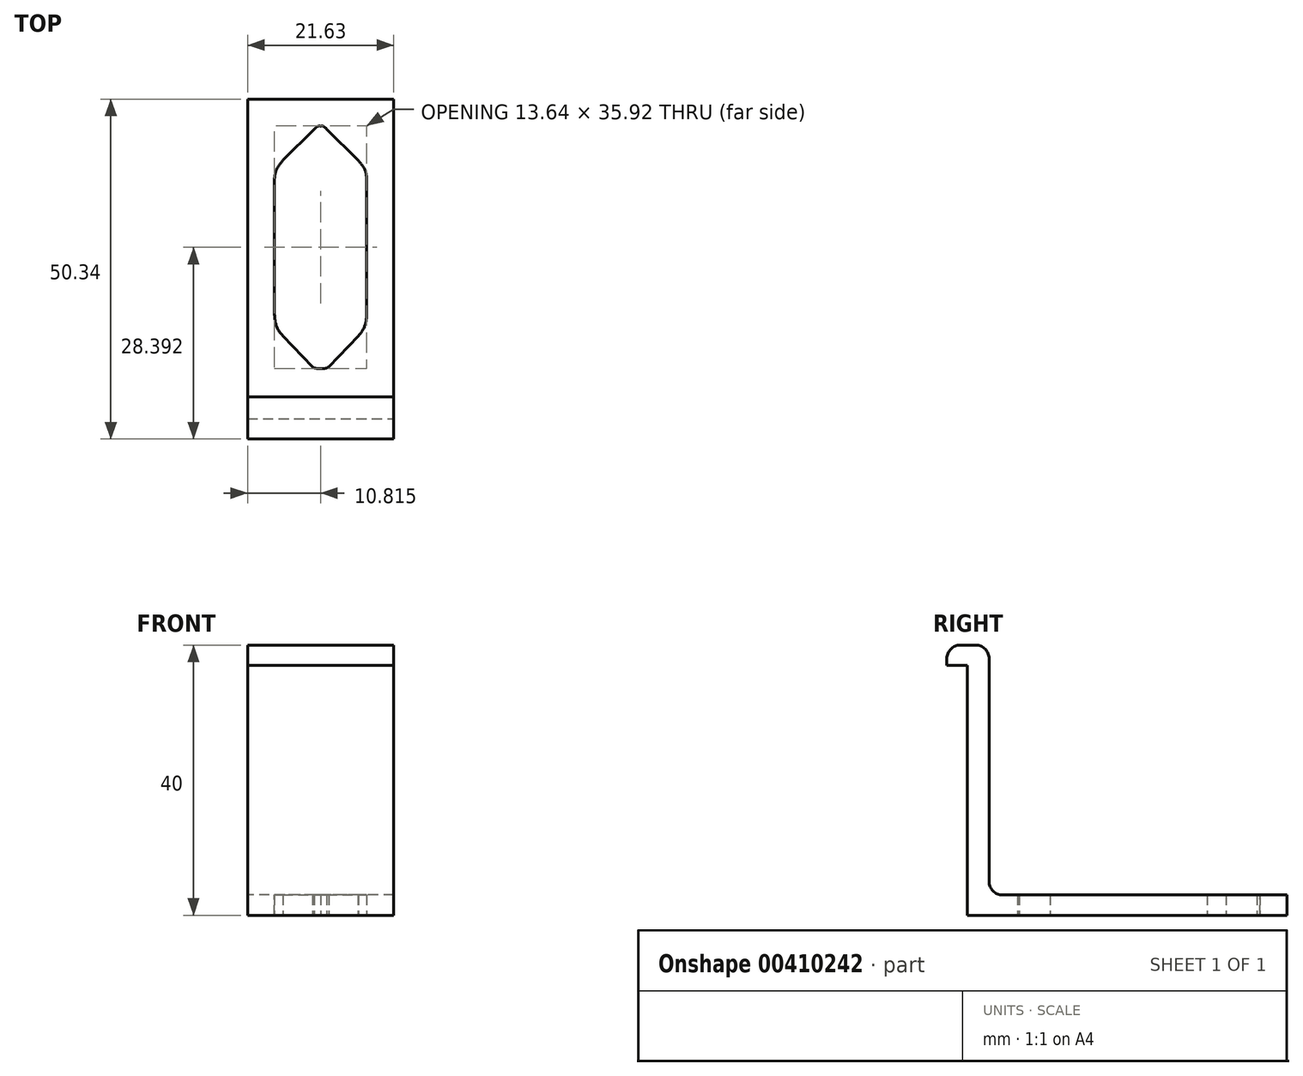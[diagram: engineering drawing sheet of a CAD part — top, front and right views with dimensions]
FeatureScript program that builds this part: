
annotation { "Feature Type Name" : "Feature", "Feature Type Description" : "" }
export const myFeature = defineFeature(function(context is Context, id is Id, definition is map)
    precondition{}
    {
        {
            var Q0;
            Q0=qCreatedBy(makeId("Top.planeOp"),FACE);
            var sketch = newSketch(context, id + "F0", { "sketchPlane" : qUnion([Q0])});
            skLineSegment(sketch, "E0", {"start": v(60.72, -23.6) * mm, "end": v(60.72, -19.6) * mm, "construction": true});
            skFitSpline(sketch, "E1", {"points": [v(60.72, 16.31) * mm, v(61.64, 15.85) * mm], "startDerivative": vector(1.57, 0.08) * mm, "endDerivative": vector(1.53, -1.37) * mm});
            skLineSegment(sketch, "E2", {"start": v(61.64, 15.85) * mm, "end": v(66.27, 11.3) * mm});
            skFitSpline(sketch, "E3", {"points": [v(66.27, 11.3) * mm, v(67.53, 8.52) * mm], "startDerivative": vector(2.41, -3.3) * mm, "endDerivative": vector(0.3, -4.44) * mm});
            skLineSegment(sketch, "E4", {"start": v(67.53, 8.52) * mm, "end": v(67.53, -11.27) * mm});
            skFitSpline(sketch, "E5", {"points": [v(67.53, -11.27) * mm, v(66.32, -14.75) * mm], "startDerivative": vector(0.03, -4.08) * mm, "endDerivative": vector(-3.06, -3.36) * mm});
            skLineSegment(sketch, "E6", {"start": v(66.32, -14.75) * mm, "end": v(61.93, -19.32) * mm});
            skFitSpline(sketch, "E7", {"points": [v(61.93, -19.32) * mm, v(60.72, -19.6) * mm], "startDerivative": vector(-1.02, -0.93) * mm, "endDerivative": vector(-1.06, -0.03) * mm});
            skLineSegment(sketch, "E8.MirrorCS", {"start": v(53.9, 8.52) * mm, "end": v(53.9, -11.27) * mm});
            skLineSegment(sketch, "E9.MirrorCS", {"start": v(59.79, 15.85) * mm, "end": v(55.16, 11.3) * mm});
            skFitSpline(sketch, "E10.MirrorCS", {"points": [v(60.72, 16.31) * mm, v(59.79, 15.85) * mm], "startDerivative": vector(-1.57, 0.08) * mm, "endDerivative": vector(-1.53, -1.37) * mm});
            skFitSpline(sketch, "E11.MirrorCS", {"points": [v(55.16, 11.3) * mm, v(53.9, 8.52) * mm], "startDerivative": vector(-2.41, -3.3) * mm, "endDerivative": vector(-0.3, -4.44) * mm});
            skFitSpline(sketch, "E12.MirrorCS", {"points": [v(53.9, -11.27) * mm, v(55.11, -14.75) * mm], "startDerivative": vector(-0.03, -4.08) * mm, "endDerivative": vector(3.06, -3.36) * mm});
            skLineSegment(sketch, "E13.MirrorCS", {"start": v(55.11, -14.75) * mm, "end": v(59.5, -19.32) * mm});
            skFitSpline(sketch, "E14.MirrorCS", {"points": [v(59.5, -19.32) * mm, v(60.72, -19.6) * mm], "startDerivative": vector(1.02, -0.93) * mm, "endDerivative": vector(1.06, -0.03) * mm});
            skLineSegment(sketch, "E15", {"start": v(67.53, -1.37) * mm, "end": v(71.53, -1.37) * mm, "construction": true});
            skLineSegment(sketch, "E16", {"start": v(71.53, -23.03) * mm, "end": v(71.53, 20.31) * mm});
            skLineSegment(sketch, "E17", {"start": v(71.53, 20.31) * mm, "end": v(60.72, 20.31) * mm});
            skLineSegment(sketch, "E18.MirrorCS", {"start": v(49.9, -23.03) * mm, "end": v(49.9, 20.31) * mm});
            skLineSegment(sketch, "E19.MirrorCS", {"start": v(49.9, 20.31) * mm, "end": v(60.72, 20.31) * mm});
            skLineSegment(sketch, "E20", {"start": v(60.72, 16.31) * mm, "end": v(60.72, 20.31) * mm, "construction": true});
            skLineSegment(sketch, "E21", {"start": v(60.72, -19.6) * mm, "end": v(60.72, 16.31) * mm, "construction": true});
            skLineSegment(sketch, "E22.top", {"start": v(49.9, -27.03) * mm, "end": v(71.53, -27.03) * mm});
            skLineSegment(sketch, "E22.left", {"start": v(49.9, -23.03) * mm, "end": v(49.9, -23.78) * mm});
            skLineSegment(sketch, "E22.right", {"start": v(71.53, -23.03) * mm, "end": v(71.53, -27.03) * mm});
            skLineSegment(sketch, "E23", {"start": v(49.9, -23.78) * mm, "end": v(71.53, -23.78) * mm});
            skLineSegment(sketch, "E24", {"start": v(49.9, -23.78) * mm, "end": v(49.9, -27.03) * mm});
            skSolve(sketch);
        }
        {
            var Q0;
            Q0=makeQuery(id+"F0.imprint","IMPRINT",FACE,{"disambiguationData":[TD([[makeQuery(id+"F0.imprint","IMPRINT",EDGE,{"derivedFrom":sQuery(id+"F0.wireOp",EDGE,"E1")}),1.0]])]});
            var Q1;
            {var subQ0=sQuery(id+"F0.wireOp",EDGE,"E22.top");Q1=makeQuery(id+"F0.imprint","IMPRINT",FACE,{"disambiguationData":[TD([[makeQuery(id+"F0.imprint","IMPRINT",EDGE,{"derivedFrom":subQ0}),1.0]])]});}
            extrude(context, id + "F1", {"entities" : qUnion([Q0, Q1]), "depth" : 3 * mm});
        }
        {
            var Q0;
            {var subQ0=sQuery(id+"F0.wireOp",EDGE,"E22.top");Q0=makeQuery(id+"F0.imprint","IMPRINT",FACE,{"disambiguationData":[TD([[makeQuery(id+"F0.imprint","IMPRINT",EDGE,{"derivedFrom":subQ0}),1.0]])]});}
            extrude(context, id + "F2", {"entities" : qUnion([Q0]), "operationType" : NewBodyOperationType.ADD, "depth" : 40 * mm});
        }
        {
            var Q0;
            {var subQ0=sQuery(id+"F0.wireOp",EDGE,"E22.top");Q0=makeQuery(id+"F2.boolean.opBoolean","MERGE",FACE,{"derivedFrom":[makeQuery(id+"F1.opExtrude","SWEPT_FACE",FACE,{"disambiguationData":[OSD([subQ0])]}),makeQuery(id+"F2.opExtrude","SWEPT_FACE",FACE,{"disambiguationData":[OSD([subQ0])]})]});}
            var sketch = newSketch(context, id + "F3", { "sketchPlane" : qUnion([Q0])});
            skLineSegment(sketch, "E25.bottom", {"start": v(49.9, 40) * mm, "end": v(71.53, 40) * mm});
            skLineSegment(sketch, "E25.top", {"start": v(49.9, 37) * mm, "end": v(71.53, 37) * mm});
            skLineSegment(sketch, "E25.left", {"start": v(49.9, 40) * mm, "end": v(49.9, 37) * mm});
            skLineSegment(sketch, "E25.right", {"start": v(71.53, 40) * mm, "end": v(71.53, 37) * mm});
            skSolve(sketch);
        }
        {
            var Q0;
            Q0 = qSketchRegion(id + "F3", true);
            extrude(context, id + "F4", {"entities" : qUnion([Q0]), "operationType" : NewBodyOperationType.ADD, "depth" : 3 * mm});
        }
        {
            var Q0;
            Q0=makeQuery(id+"F4.opExtrude","CAP_EDGE",EDGE,{"disambiguationData":[OSD([sQuery(id+"F3.wireOp",EDGE,"E25.bottom")])],"isStart":false});
            var Q1;
            Q1=makeQuery(id+"F2.opExtrude","CAP_EDGE",EDGE,{"disambiguationData":[OSD([sQuery(id+"F0.wireOp",EDGE,"E23")])],"isStart":false});
            var Q2;
            Q2=makeQuery(id+"F2.boolean.opBoolean","INTERSECT",EDGE,{"derivedFrom":[makeQuery(id+"F1.opExtrude","CAP_FACE",FACE,{"disambiguationData":[OSD([sQuery(id+"F0.wireOp",EDGE,"E1"),sQuery(id+"F0.wireOp",EDGE,"E2"),sQuery(id+"F0.wireOp",EDGE,"E3"),sQuery(id+"F0.wireOp",EDGE,"E4"),sQuery(id+"F0.wireOp",EDGE,"E5"),sQuery(id+"F0.wireOp",EDGE,"E6"),sQuery(id+"F0.wireOp",EDGE,"E7"),sQuery(id+"F0.wireOp",EDGE,"E8.MirrorCS"),sQuery(id+"F0.wireOp",EDGE,"E9.MirrorCS"),sQuery(id+"F0.wireOp",EDGE,"E10.MirrorCS"),sQuery(id+"F0.wireOp",EDGE,"E11.MirrorCS"),sQuery(id+"F0.wireOp",EDGE,"E12.MirrorCS"),sQuery(id+"F0.wireOp",EDGE,"E13.MirrorCS"),sQuery(id+"F0.wireOp",EDGE,"E14.MirrorCS"),sQuery(id+"F0.wireOp",EDGE,"E16"),sQuery(id+"F0.wireOp",EDGE,"E17"),sQuery(id+"F0.wireOp",EDGE,"E18.MirrorCS"),sQuery(id+"F0.wireOp",EDGE,"E19.MirrorCS"),sQuery(id+"F0.wireOp",EDGE,"E22.top"),sQuery(id+"F0.wireOp",EDGE,"E22.left"),sQuery(id+"F0.wireOp",EDGE,"E22.right"),sQuery(id+"F0.wireOp",EDGE,"E24")])],"isStart":false}),makeQuery(id+"F2.opExtrude","SWEPT_FACE",FACE,{"disambiguationData":[OSD([sQuery(id+"F0.wireOp",EDGE,"E23")])]})]});
            fillet(context, id + "F5", {"entities" : qUnion([Q0, Q1, Q2]), "radius" : 2 * mm, "tangentPropagation" : true, "allowEdgeOverflow" : false});
        }
    });
